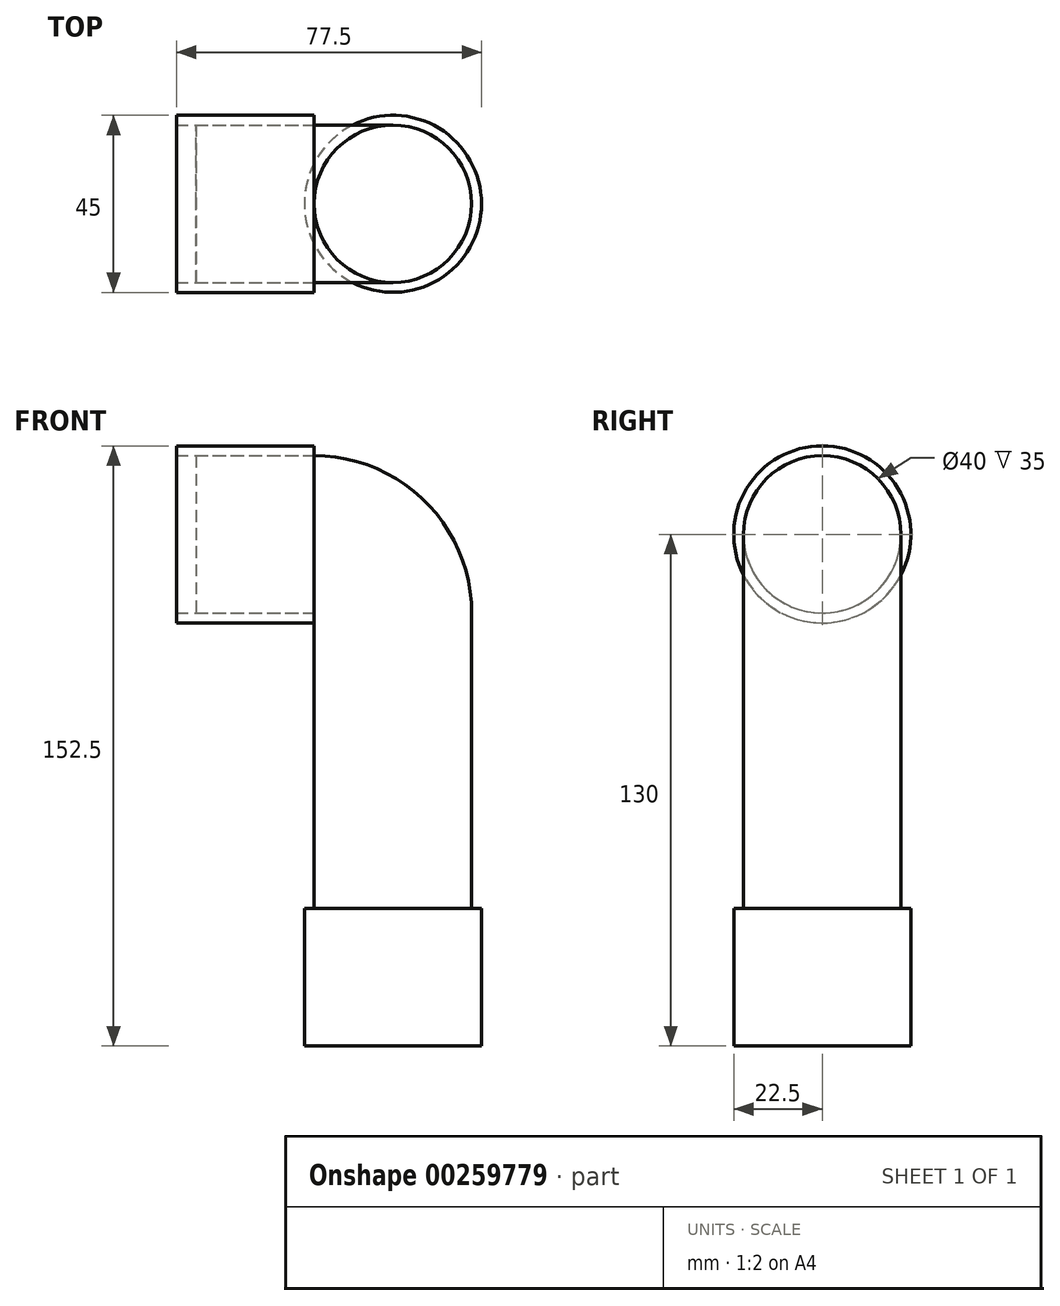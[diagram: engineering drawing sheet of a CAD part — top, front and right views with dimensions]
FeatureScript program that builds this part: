
annotation { "Feature Type Name" : "Feature", "Feature Type Description" : "" }
export const myFeature = defineFeature(function(context is Context, id is Id, definition is map)
    precondition{}
    {
        {
            var Q0;
            Q0=qCreatedBy(makeId("Front.planeOp"),FACE);
            var sketch = newSketch(context, id + "F0", { "sketchPlane" : qUnion([Q0])});
            skLineSegment(sketch, "E0", {"start": v(0, 0) * mm, "end": v(0, 110) * mm});
            skLineSegment(sketch, "E1", {"start": v(0, 110) * mm, "end": v(-20, 110) * mm, "construction": true});
            skArc(sketch, "E2", {"start": v(0, 110) * mm, "mid": v(-5.86, 124.14) * mm, "end": v(-20, 130) * mm});
            skSolve(sketch);
        }
        {
            var Q0;
            Q0=qCreatedBy(makeId("Top.planeOp"),FACE);
            var sketch = newSketch(context, id + "F1", { "sketchPlane" : qUnion([Q0])});
            skCircle(sketch, "E3", {"center": v(0, 0) * mm, "radius": 20 * mm});
            skSolve(sketch);
        }
        {
            var Q0;
            Q0=makeQuery(id+"F1.imprint","IMPRINT",FACE,{"disambiguationData":[TD([[makeQuery(id+"F1.imprint","IMPRINT",EDGE,{"derivedFrom":sQuery(id+"F1.wireOp",EDGE,"E3")}),1.0]])]});
            var Q1;
            Q1=sQuery(id+"F0.wireOp",EDGE,"E2");
            var Q2;
            Q2=sQuery(id+"F0.wireOp",EDGE,"E0");
            sweep(context, id + "F2", {"profiles" : qUnion([Q0]), "path" : qUnion([Q1, Q2])});
        }
        {
            var Q0;
            Q0=qCreatedBy(makeId("Top.planeOp"),FACE);
            var sketch = newSketch(context, id + "F3", { "sketchPlane" : qUnion([Q0])});
            skCircle(sketch, "E4", {"center": v(0, 0) * mm, "radius": 22.5 * mm});
            skSolve(sketch);
        }
        {
            var Q0;
            Q0=makeQuery(id+"F3.imprint","IMPRINT",FACE,{"disambiguationData":[TD([[makeQuery(id+"F3.imprint","IMPRINT",EDGE,{"derivedFrom":sQuery(id+"F3.wireOp",EDGE,"E4")}),1.0]])]});
            extrude(context, id + "F4", {"entities" : qUnion([Q0]), "operationType" : NewBodyOperationType.ADD, "depth" : 35 * mm});
        }
        {
            var Q0;
            Q0=makeQuery(id+"F2.opSweep","CAP_FACE",FACE,{"disambiguationData":[OSD([sQuery(id+"F0.wireOp",VERTEX,"E2.end"),sQuery(id+"F1.wireOp",EDGE,"E3")])],"isStart":false});
            var sketch = newSketch(context, id + "F5", { "sketchPlane" : qUnion([Q0])});
            skCircle(sketch, "E5", {"center": v(0, 130) * mm, "radius": 22.5 * mm});
            skSolve(sketch);
        }
        {
            var Q0;
            Q0=makeQuery(id+"F5.imprint","IMPRINT",FACE,{"disambiguationData":[TD([[makeQuery(id+"F5.imprint","IMPRINT",EDGE,{"derivedFrom":sQuery(id+"F5.wireOp",EDGE,"E5")}),1.0]])]});
            extrude(context, id + "F6", {"entities" : qUnion([Q0]), "operationType" : NewBodyOperationType.ADD, "depth" : 35 * mm});
        }
        {
            var Q0;
            Q0=makeQuery(id+"F2.opSweep","CAP_FACE",FACE,{"disambiguationData":[OSD([sQuery(id+"F0.wireOp",VERTEX,"E2.end"),sQuery(id+"F1.wireOp",EDGE,"E3")])],"isStart":false});
            extrude(context, id + "F7", {"entities" : qUnion([Q0]), "depth" : 30 * mm});
        }
    });
